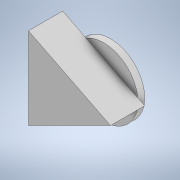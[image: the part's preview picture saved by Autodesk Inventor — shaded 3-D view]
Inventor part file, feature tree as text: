
AUTODESK INVENTOR PART (.ipt)
format: ipt  version: 2020.1 (Build 241239000, 239)  size: 105,984 bytes
history: native  units: mm
features: extrude x2, sketch x2
ambient origin geometry x8: Origin, YZ Plane, XZ Plane, XY Plane, X Axis, Y Axis, Z Axis, Center Point
bodies: Body1 (feature_tree)
feature tree (4):
  extrude  "Extrusion4"  Depth=10.0mm
  extrude  "Extrusion5"  [1 undecoded]
  sketch  "Sketch3"  dims[d12=5.0mm d13=0.0mm d16=10.0mm]
  sketch  "Sketch4"  dims[d17=1.0mm d18=0.0mm]
note: 1 required parameter value undecoded (feature->parameter linkage not recoverable at this tier; creation-order binding heuristic only, values carry confidence <= 0.55)
